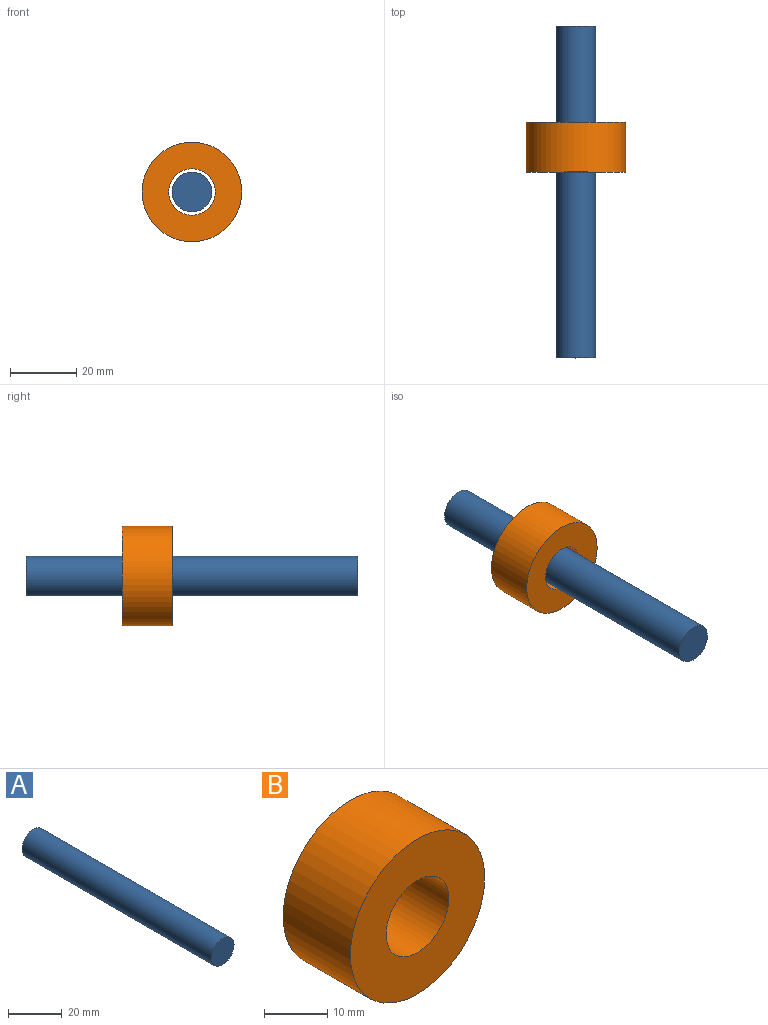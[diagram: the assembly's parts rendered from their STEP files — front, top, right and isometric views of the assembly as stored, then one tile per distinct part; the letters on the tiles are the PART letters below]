
ASSEMBLY  parts=2 mates=1
PART A: 3 faces, bbox 12x100x12 mm
  f0: cylinder r=6mm len=100mm, axis (0,-1,0), area 3769.9mm2, adj f1,f2
  f1: plane 12x12mm, normal (0,1,0), area 113.1mm2, adj f0
  f2: plane 12x12mm, normal (0,-1,0), area 113.1mm2, adj f0
PART B: 4 faces, bbox 30x15x30 mm
  f0: cylinder r=7mm len=15mm, axis (0,-1,0), area 659.7mm2, adj f2,f3
  f1: cylinder r=15mm len=30mm, axis (0,-1,0), area 1413.7mm2, adj f2,f3
  f2: plane 30x30mm, normal (0,1,0), area 552.9mm2, adj f0,f1
  f3: plane 30x30mm, normal (0,-1,0), area 552.9mm2, adj f0,f1
PLACE A t=(9.02,-26.91,26.83)mm fixed
PLACE B t=(9.02,29.09,26.83)mm
MATE cylindrical B.f0 <-> A.f0  axis (0,-1,0) through (9.02,29.09,26.83)mm
